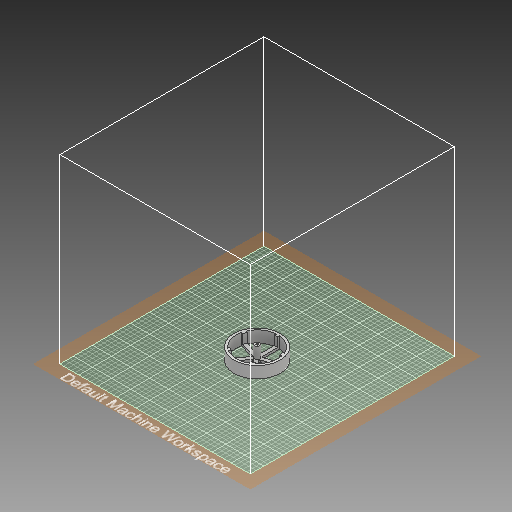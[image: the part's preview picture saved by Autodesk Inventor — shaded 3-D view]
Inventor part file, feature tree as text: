
AUTODESK INVENTOR PART (.ipt)
format: ipt  version: 2019 (Build 230136000, 136)  size: 482,816 bytes
history: native  units: in
note: dims shown in document units (in); Inventor stores cm internally (conversion verified against a paired STEP export)
features: sketch x6, extrude x5, fillet x2, other x1, rib x1, pattern_circular x1
ambient origin geometry x8: Origin, YZ Plane, XZ Plane, XY Plane, X Axis, Y Axis, Z Axis, Center Point
bodies: Solid1 (feature_tree)
feature tree (16):
  other  "CrossSection1"
  extrude  "Extrusion1"  Depth=1.0in TaperAngle=0.0deg
  extrude  "Extrusion2"  Depth=0.45in
  extrude  "Extrusion3"  Depth=0.2in TaperAngle=0.0deg
  extrude  "Extrusion4"  Depth=0.14in
  extrude  "Extrusion5"  Depth=0.1in
  rib  "Rib1"
  pattern_circular  "Circular Pattern1"  [2 undecoded]
  fillet  "Fillet1"  Radius=1.9685in
  fillet  "Fillet2"  Radius=1.0in
  sketch  "Sketch1"  dims[d0=3.9in d1=1.0in d2=0.0in]
  sketch  "Sketch2"  dims[d3=0.35in d4=0.45in]
  sketch  "Sketch3"  dims[d5=0.8in d6=0.0in d7=0.2in d8=0.0in]
  sketch  "Sketch4"  dims[d9=0.2in d10=0.14in]
  sketch  "Sketch5"  dims[d11=0.3in d12=0.0in d13=0.1in]
  sketch  "Sketch8"  dims[d14=0.2in d16=0.3in d17=1.9685in d19=360.0deg d21=1.0in d22=0.0in d23=0.013in d24=0.5in d25=0.0in d26=2.0in d27=0.1in d28=0.1in d29=0.0in d30=0.0in d31=0.1in d32=0.1in d33=1.9685in d34=360.0deg d36=0.125in d37=0.125in]
note: 2 required parameter values undecoded (feature->parameter linkage not recoverable at this tier; creation-order binding heuristic only, values carry confidence <= 0.55)
